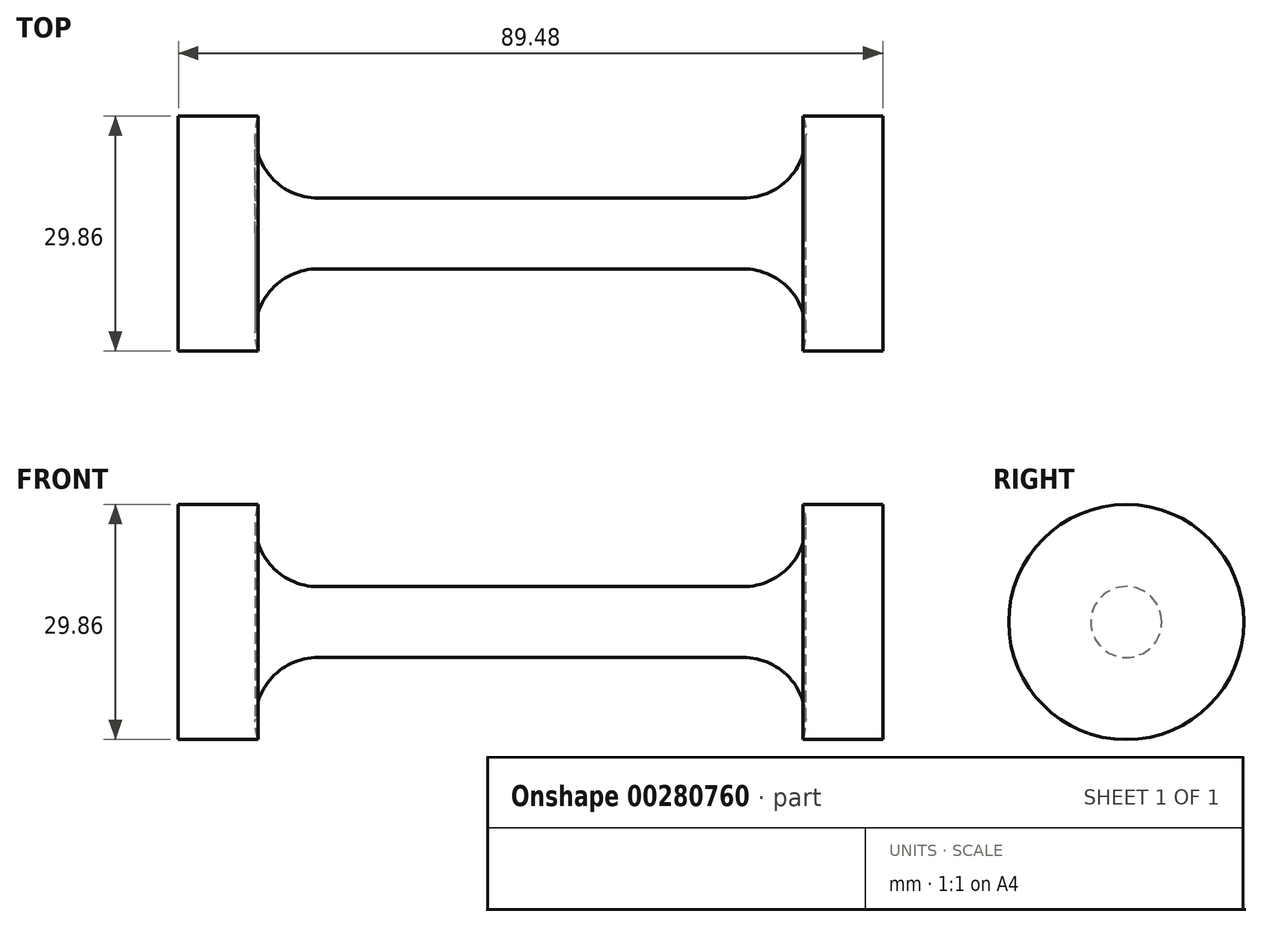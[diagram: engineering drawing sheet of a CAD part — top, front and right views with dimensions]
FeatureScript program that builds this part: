
annotation { "Feature Type Name" : "Feature", "Feature Type Description" : "" }
export const myFeature = defineFeature(function(context is Context, id is Id, definition is map)
    precondition{}
    {
        {
            var Q0;
            Q0=qCreatedBy(makeId("Front.planeOp"),FACE);
            var sketch = newSketch(context, id + "F0", { "sketchPlane" : qUnion([Q0])});
            skLineSegment(sketch, "E0", {"start": v(0, 4.5) * mm, "end": v(27, 4.5) * mm});
            skArc(sketch, "E1", {"start": v(27, 4.5) * mm, "mid": v(33.46, 7.78) * mm, "end": v(34.62, 14.93) * mm});
            skLineSegment(sketch, "E2", {"start": v(34.62, 14.93) * mm, "end": v(44.74, 14.93) * mm});
            skLineSegment(sketch, "E3", {"start": v(44.74, 14.93) * mm, "end": v(44.74, 0) * mm});
            skLineSegment(sketch, "E4.MirrorCS", {"start": v(-34.62, 14.93) * mm, "end": v(-44.74, 14.93) * mm});
            skArc(sketch, "E5.MirrorCS", {"start": v(-27, 4.5) * mm, "mid": v(-33.46, 7.78) * mm, "end": v(-34.62, 14.93) * mm});
            skLineSegment(sketch, "E6.MirrorCS", {"start": v(0, 4.5) * mm, "end": v(-27, 4.5) * mm});
            skLineSegment(sketch, "E7.MirrorCS", {"start": v(-44.74, 14.93) * mm, "end": v(-44.74, 0) * mm});
            skLineSegment(sketch, "E8", {"start": v(-44.74, 0) * mm, "end": v(44.74, 0) * mm});
            skSolve(sketch);
        }
        {
            var Q0;
            Q0 = qSketchRegion(id + "F0", true);
            var Q1;
            Q1=sQuery(id+"F0.wireOp",EDGE,"E8");
            revolve(context, id + "F1", {"entities" : qUnion([Q0]), "axis" : qUnion([Q1]), "revolveType" : RevolveType.FULL});
        }
    });
